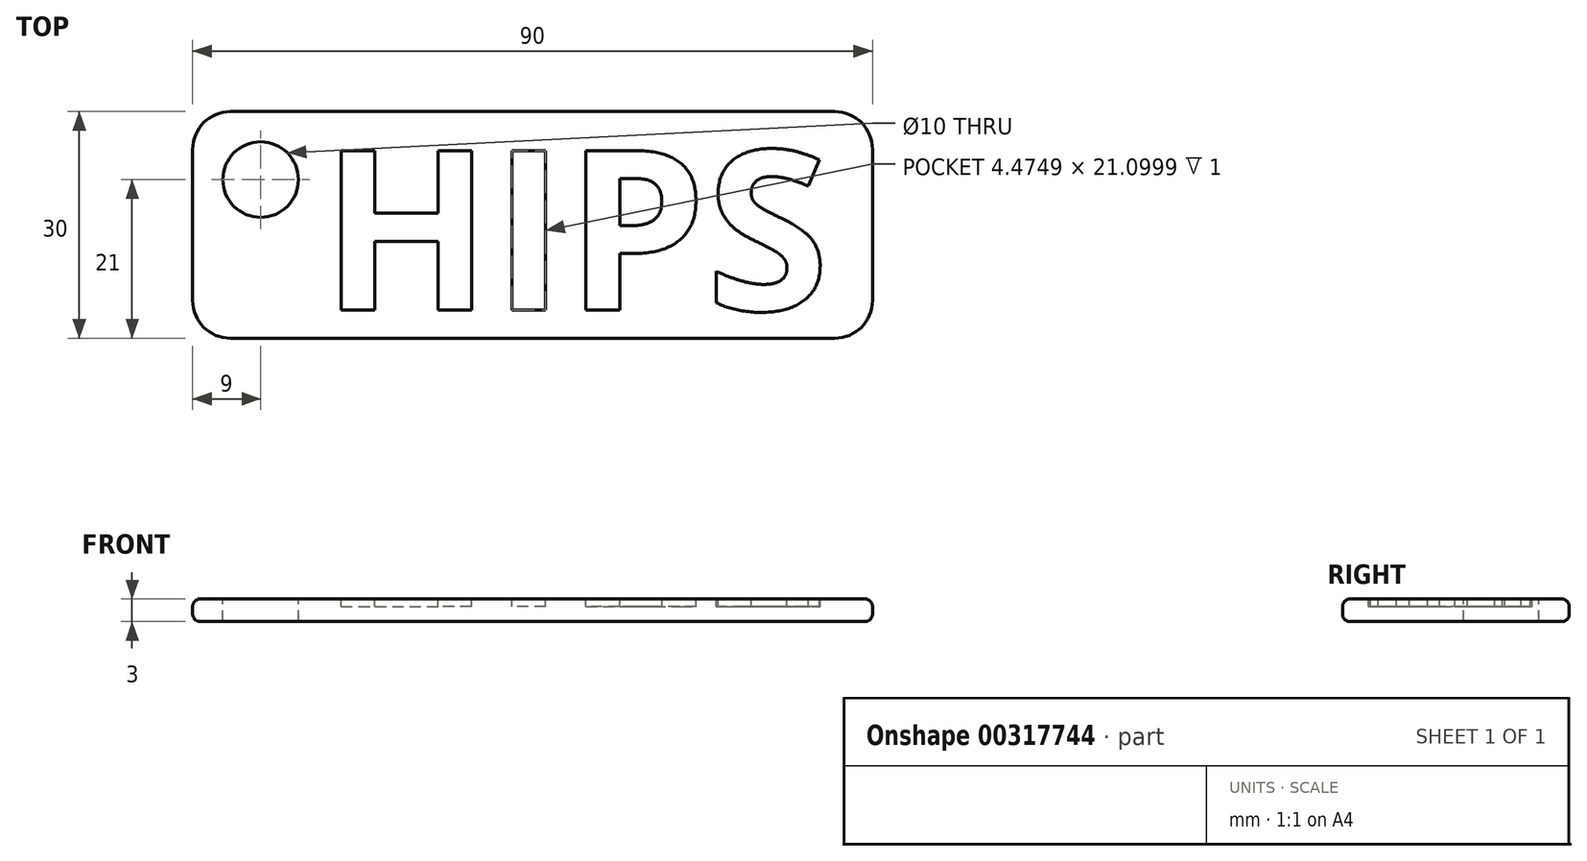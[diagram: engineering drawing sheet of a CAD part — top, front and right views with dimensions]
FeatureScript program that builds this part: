
annotation { "Feature Type Name" : "Feature", "Feature Type Description" : "" }
export const myFeature = defineFeature(function(context is Context, id is Id, definition is map)
    precondition{}
    {
        {
            var Q0;
            Q0=qCreatedBy(makeId("Top.planeOp"),FACE);
            var sketch = newSketch(context, id + "F0", { "sketchPlane" : qUnion([Q0])});
            skLineSegment(sketch, "E0.bottom", {"start": v(-45, 15) * mm, "end": v(45, 15) * mm});
            skLineSegment(sketch, "E0.top", {"start": v(-45, -15) * mm, "end": v(45, -15) * mm});
            skLineSegment(sketch, "E0.left", {"start": v(-45, 15) * mm, "end": v(-45, -15) * mm});
            skLineSegment(sketch, "E0.right", {"start": v(45, 15) * mm, "end": v(45, -15) * mm});
            skLineSegment(sketch, "E1", {"start": v(-45, 15) * mm, "end": v(45, -15) * mm, "construction": true});
            skSolve(sketch);
        }
        {
            var Q0;
            Q0=makeQuery(id+"F0.imprint","IMPRINT",FACE,{"disambiguationData":[TD([[makeQuery(id+"F0.imprint","IMPRINT",EDGE,{"derivedFrom":sQuery(id+"F0.wireOp",EDGE,"E0.bottom")}),-1.0]])]});
            extrude(context, id + "F1", {"entities" : qUnion([Q0]), "depth" : 3 * mm});
        }
        {
            var Q0;
            Q0=makeQuery(id+"F1.opExtrude","CAP_FACE",FACE,{"disambiguationData":[OSD([sQuery(id+"F0.wireOp",EDGE,"E0.bottom"),sQuery(id+"F0.wireOp",EDGE,"E0.top"),sQuery(id+"F0.wireOp",EDGE,"E0.left"),sQuery(id+"F0.wireOp",EDGE,"E0.right")])],"isStart":false});
            var Q1;
            Q1=makeQuery(id+"F1.opExtrude","CAP_FACE",FACE,{"disambiguationData":[OSD([sQuery(id+"F0.wireOp",EDGE,"E0.bottom"),sQuery(id+"F0.wireOp",EDGE,"E0.top"),sQuery(id+"F0.wireOp",EDGE,"E0.left"),sQuery(id+"F0.wireOp",EDGE,"E0.right")])],"isStart":true});
            fillet(context, id + "F2", {"entities" : qUnion([Q0, Q1]), "radius" : 1 * mm, "tangentPropagation" : true, "allowEdgeOverflow" : false});
        }
        {
            var Q0;
            Q0=makeQuery(id+"F1.opExtrude","SWEPT_EDGE",EDGE,{"disambiguationData":[OSD([sQuery(id+"F0.wireOp",EDGE,"E0.top"),sQuery(id+"F0.wireOp",EDGE,"E0.right")])]});
            var Q1;
            Q1=makeQuery(id+"F1.opExtrude","SWEPT_EDGE",EDGE,{"disambiguationData":[OSD([sQuery(id+"F0.wireOp",EDGE,"E0.bottom"),sQuery(id+"F0.wireOp",EDGE,"E0.right")])]});
            var Q2;
            Q2=makeQuery(id+"F1.opExtrude","SWEPT_EDGE",EDGE,{"disambiguationData":[OSD([sQuery(id+"F0.wireOp",EDGE,"E0.bottom"),sQuery(id+"F0.wireOp",EDGE,"E0.left")])]});
            var Q3;
            Q3=makeQuery(id+"F1.opExtrude","SWEPT_EDGE",EDGE,{"disambiguationData":[OSD([sQuery(id+"F0.wireOp",EDGE,"E0.top"),sQuery(id+"F0.wireOp",EDGE,"E0.left")])]});
            fillet(context, id + "F3", {"entities" : qUnion([Q0, Q1, Q2, Q3]), "radius" : 5 * mm, "tangentPropagation" : true, "allowEdgeOverflow" : false});
        }
        {
            var Q0;
            {var subQ0=sQuery(id+"F0.wireOp",EDGE,"E0.left");var subQ2=sQuery(id+"F0.wireOp",EDGE,"E0.bottom");var subQ4=sQuery(id+"F0.wireOp",EDGE,"E0.right");var subQ6=sQuery(id+"F0.wireOp",EDGE,"E0.top");Q0=makeQuery(id+"FmQCBBX3Ub0qneL_1.boolean.opBoolean","SPLIT",FACE,{"disambiguationData":[TD([makeQuery(id+"FmQCBBX3Ub0qneL_1.opExtrude","SWEPT_FACE",FACE,{"disambiguationData":[OSD([sQuery(id+"FOCoeRmDbjhRCuz_1.wireOp",EDGE,"4a1fb44a-e7be-4e23-9449-000d953c446c.sketch_text.stroke-0")])]})])],"derivedFrom":makeQuery(id+"F1.opExtrude","CAP_FACE",FACE,{"disambiguationData":[OSD([subQ2,subQ6,subQ0,subQ4])],"isStart":false})});}
            var sketch = newSketch(context, id + "F4", { "sketchPlane" : qUnion([Q0])});
            skCircle(sketch, "E2", {"center": v(-36, 6) * mm, "radius": 5 * mm});
            skSolve(sketch);
        }
        {
            var Q0;
            Q0=qSketchRegion(id+"F4",true);
            extrude(context, id + "F5", {"entities" : qUnion([Q0]), "operationType" : NewBodyOperationType.REMOVE, "oppositeDirection" : true, "depth" : 3 * mm});
        }
        {
            var Q0;
            Q0=makeQuery(id+"F1.opExtrude","CAP_FACE",FACE,{"disambiguationData":[OSD([sQuery(id+"F0.wireOp",EDGE,"E0.bottom"),sQuery(id+"F0.wireOp",EDGE,"E0.top"),sQuery(id+"F0.wireOp",EDGE,"E0.left"),sQuery(id+"F0.wireOp",EDGE,"E0.right")])],"isStart":false});
            var sketch = newSketch(context, id + "F6", { "sketchPlane" : qUnion([Q0])});
            skText(sketch, "E3", { "text": "HIPS", "fontName": "OpenSans-Bold.ttf"});
            const initialGuessF6  = {"E3": [-0.028, -0.01128, 1, 0, 0.02128]};
            skSetInitialGuess(sketch, initialGuessF6);
            skSolve(sketch);
        }
        {
            var Q0;
            Q0=qSketchRegion(id+"F6",true);
            extrude(context, id + "F7", {"entities" : qUnion([Q0]), "operationType" : NewBodyOperationType.REMOVE, "oppositeDirection" : true, "depth" : 1 * mm});
        }
    });
